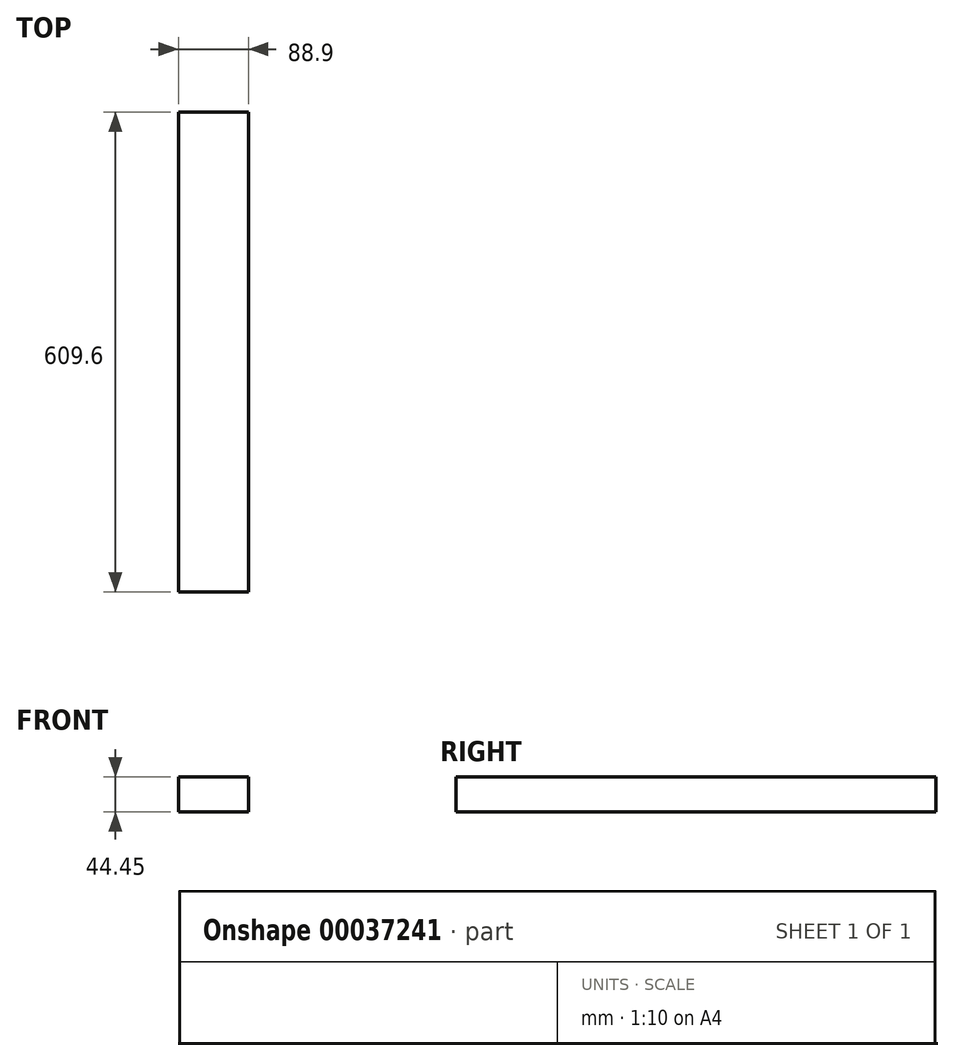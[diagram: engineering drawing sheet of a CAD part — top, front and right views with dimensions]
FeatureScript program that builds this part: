
annotation { "Feature Type Name" : "Feature", "Feature Type Description" : "" }
export const myFeature = defineFeature(function(context is Context, id is Id, definition is map)
    precondition{}
    {
        {
            var Q0;
            Q0=qCreatedBy(makeId("Front.planeOp"),FACE);
            var sketch = newSketch(context, id + "F0", { "sketchPlane" : qUnion([Q0])});
            skLineSegment(sketch, "E0.bottom", {"start": v(0, 0) * mm, "end": v(88.9, 0) * mm});
            skLineSegment(sketch, "E0.top", {"start": v(0, 44.45) * mm, "end": v(88.9, 44.45) * mm});
            skLineSegment(sketch, "E0.left", {"start": v(0, 0) * mm, "end": v(0, 44.45) * mm});
            skLineSegment(sketch, "E0.right", {"start": v(88.9, 0) * mm, "end": v(88.9, 44.45) * mm});
            skSolve(sketch);
        }
        {
            var Q0;
            Q0=makeQuery(id+"F0.imprint","IMPRINT",FACE,{"disambiguationData":[TD([[makeQuery(id+"F0.imprint","IMPRINT",EDGE,{"derivedFrom":sQuery(id+"F0.wireOp",EDGE,"E0.bottom")}),1.0]])]});
            extrude(context, id + "F1", {"entities" : qUnion([Q0]), "depth" : 609.6 * mm});
        }
    });
